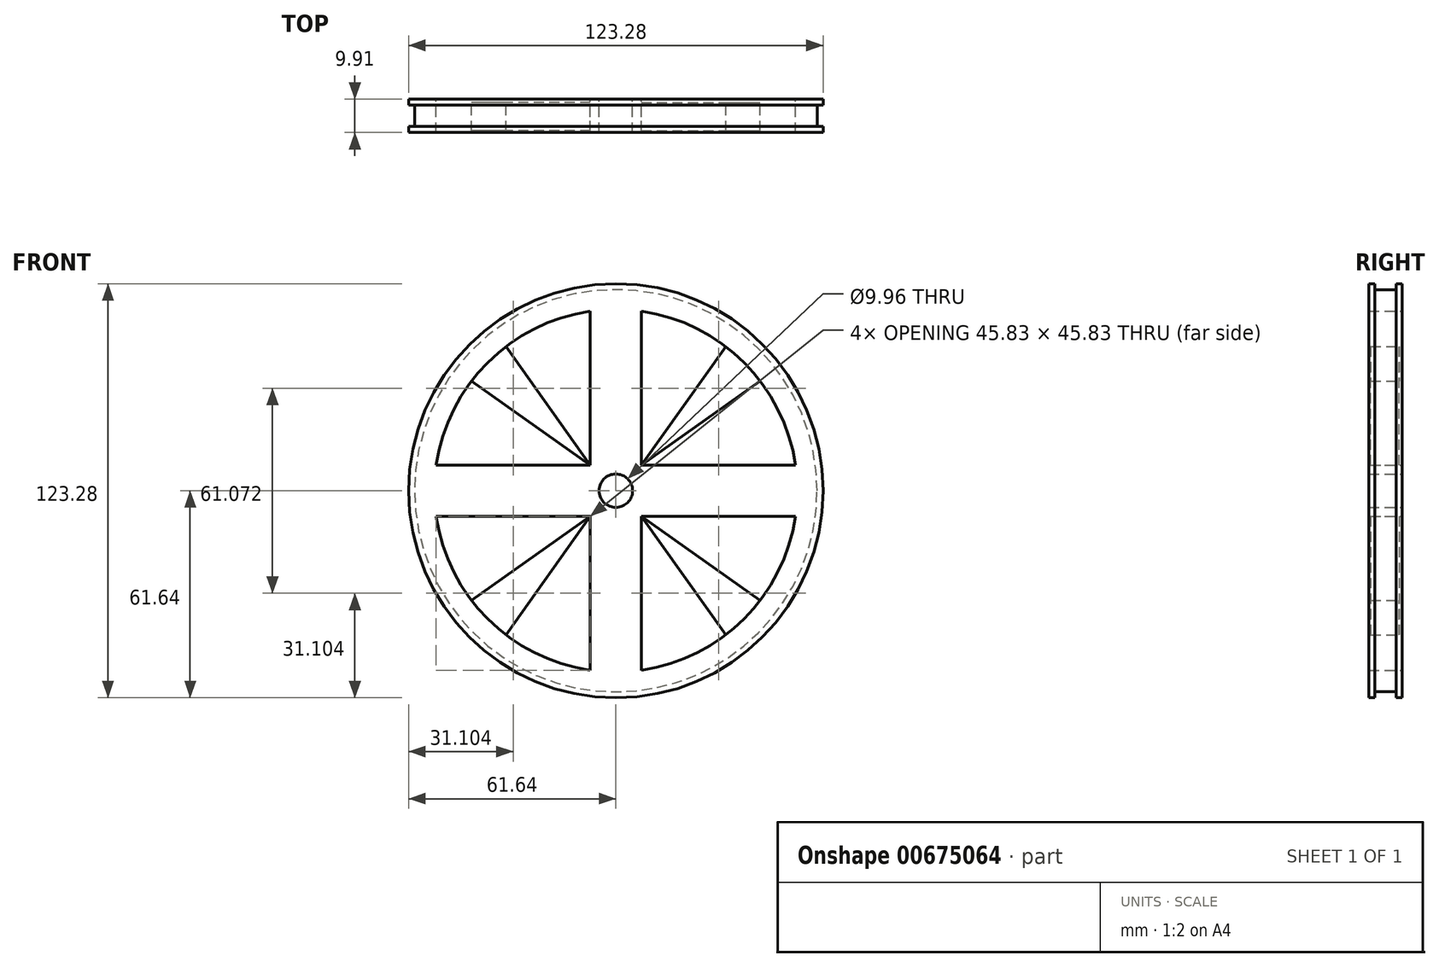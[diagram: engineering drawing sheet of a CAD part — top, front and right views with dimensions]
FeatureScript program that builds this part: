
annotation { "Feature Type Name" : "Feature", "Feature Type Description" : "" }
export const myFeature = defineFeature(function(context is Context, id is Id, definition is map)
    precondition{}
    {
        {
            var Q0;
            Q0=qCreatedBy(makeId("Front.planeOp"),FACE);
            var sketch = newSketch(context, id + "F0", { "sketchPlane" : qUnion([Q0])});
            skCircle(sketch, "E0", {"center": v(0, 0) * mm, "radius": 61.64 * mm});
            skLineSegment(sketch, "E1", {"start": v(-61.64, 0) * mm, "end": v(0, 0) * mm});
            skLineSegment(sketch, "E2", {"start": v(0, 0) * mm, "end": v(0, 61.64) * mm});
            skPoint(sketch, "E3", {"position": v(-61.64, 0) * mm});
            skPoint(sketch, "E4", {"position": v(0, 61.64) * mm});
            skArc(sketch, "E5", {"start": v(0, 61.64) * mm, "mid": v(-43.52, 43.52) * mm, "end": v(-61.64, 0) * mm});
            skArc(sketch, "E6.0", {"start": v(-7.62, 53.45) * mm, "mid": v(-38.14, 38.14) * mm, "end": v(-53.45, 7.62) * mm});
            skLineSegment(sketch, "E6.1", {"start": v(-7.62, 7.62) * mm, "end": v(-7.62, 53.45) * mm});
            skLineSegment(sketch, "E6.2", {"start": v(-53.45, 7.62) * mm, "end": v(-7.62, 7.62) * mm});
            skArc(sketch, "E7.1.0", {"start": v(-53.45, -7.62) * mm, "mid": v(-38.14, -38.14) * mm, "end": v(-7.62, -53.45) * mm});
            skLineSegment(sketch, "E7.1.1", {"start": v(-7.62, -7.62) * mm, "end": v(-53.45, -7.62) * mm});
            skLineSegment(sketch, "E7.1.2", {"start": v(-7.62, -53.45) * mm, "end": v(-7.62, -7.62) * mm});
            skArc(sketch, "E7.2.0", {"start": v(7.62, -53.45) * mm, "mid": v(38.14, -38.14) * mm, "end": v(53.45, -7.62) * mm});
            skLineSegment(sketch, "E7.2.1", {"start": v(7.62, -7.62) * mm, "end": v(7.62, -53.45) * mm});
            skLineSegment(sketch, "E7.2.2", {"start": v(53.45, -7.62) * mm, "end": v(7.62, -7.62) * mm});
            skArc(sketch, "E7.3.0", {"start": v(53.45, 7.62) * mm, "mid": v(38.14, 38.14) * mm, "end": v(7.62, 53.45) * mm});
            skLineSegment(sketch, "E7.3.1", {"start": v(7.62, 7.62) * mm, "end": v(53.45, 7.62) * mm});
            skLineSegment(sketch, "E7.3.2", {"start": v(7.62, 53.45) * mm, "end": v(7.62, 7.62) * mm});
            skLineSegment(sketch, "E8", {"start": v(-7.62, 7.62) * mm, "end": v(-32.68, 42.9) * mm});
            skLineSegment(sketch, "E9", {"start": v(-7.62, 7.62) * mm, "end": v(-42.9, 32.68) * mm});
            skLineSegment(sketch, "E10.1.0", {"start": v(-7.62, -7.62) * mm, "end": v(-42.9, -32.68) * mm});
            skLineSegment(sketch, "E10.1.1", {"start": v(-7.62, -7.62) * mm, "end": v(-32.68, -42.9) * mm});
            skLineSegment(sketch, "E10.2.0", {"start": v(7.62, -7.62) * mm, "end": v(32.68, -42.9) * mm});
            skLineSegment(sketch, "E10.2.1", {"start": v(7.62, -7.62) * mm, "end": v(42.9, -32.68) * mm});
            skLineSegment(sketch, "E10.3.0", {"start": v(7.62, 7.62) * mm, "end": v(42.9, 32.68) * mm});
            skLineSegment(sketch, "E10.3.1", {"start": v(7.62, 7.62) * mm, "end": v(32.68, 42.9) * mm});
            skSolve(sketch);
        }
        {
            var Q0;
            Q0=makeQuery(id+"F0.imprint","IMPRINT",FACE,{"disambiguationData":[TD([[makeQuery(id+"F0.imprint","IMPRINT",EDGE,{"derivedFrom":sQuery(id+"F0.wireOp",EDGE,"E1")}),1.0]])]});
            var Q1;
            {var subQ1=sQuery(id+"F0.wireOp",EDGE,"E1");Q1=makeQuery(id+"F0.imprint","IMPRINT",FACE,{"disambiguationData":[TD([[makeQuery(id+"F0.imprint","IMPRINT",EDGE,{"derivedFrom":subQ1}),-1.0]])]});}
            extrude(context, id + "F1", {"entities" : qUnion([Q0, Q1]), "depth" : 9.9 * mm, "offsetDistance" : 25.4 * mm});
        }
        {
            var Q0;
            Q0=makeQuery(id+"F1.opExtrude","CAP_FACE",FACE,{"disambiguationData":[OSD([sQuery(id+"F0.wireOp",EDGE,"E0"),sQuery(id+"F0.wireOp",EDGE,"E5"),sQuery(id+"F0.wireOp",EDGE,"E6.0"),sQuery(id+"F0.wireOp",EDGE,"E6.1"),sQuery(id+"F0.wireOp",EDGE,"E6.2"),sQuery(id+"F0.wireOp",EDGE,"E7.1.0"),sQuery(id+"F0.wireOp",EDGE,"E7.1.1"),sQuery(id+"F0.wireOp",EDGE,"E7.1.2"),sQuery(id+"F0.wireOp",EDGE,"E7.2.0"),sQuery(id+"F0.wireOp",EDGE,"E7.2.1"),sQuery(id+"F0.wireOp",EDGE,"E7.2.2"),sQuery(id+"F0.wireOp",EDGE,"E7.3.0"),sQuery(id+"F0.wireOp",EDGE,"E7.3.1"),sQuery(id+"F0.wireOp",EDGE,"E7.3.2")])],"isStart":true});
            var sketch = newSketch(context, id + "F2", { "sketchPlane" : qUnion([Q0])});
            skCircle(sketch, "E11", {"center": v(0, 0) * mm, "radius": 4.98 * mm});
            skSolve(sketch);
        }
        {
            var Q0;
            Q0=makeQuery(id+"F2.imprint","IMPRINT",FACE,{"disambiguationData":[TD([[makeQuery(id+"F2.imprint","IMPRINT",EDGE,{"derivedFrom":sQuery(id+"F2.wireOp",EDGE,"E11")}),1.0]])]});
            extrude(context, id + "F3", {"entities" : qUnion([Q0]), "operationType" : NewBodyOperationType.REMOVE, "oppositeDirection" : true, "depth" : 25.4 * mm, "offsetDistance" : 25.4 * mm});
        }
        {
            var Q0;
            {var subQ0=sQuery(id+"F0.wireOp",EDGE,"E8");Q0=makeQuery(id+"F0.imprint","IMPRINT",FACE,{"disambiguationData":[TD([[makeQuery(id+"F0.imprint","IMPRINT",EDGE,{"derivedFrom":subQ0}),1.0]])]});}
            var Q1;
            {var subQ0=sQuery(id+"F0.wireOp",EDGE,"E10.1.0");Q1=makeQuery(id+"F0.imprint","IMPRINT",FACE,{"disambiguationData":[TD([[makeQuery(id+"F0.imprint","IMPRINT",EDGE,{"derivedFrom":subQ0}),1.0]])]});}
            var Q2;
            {var subQ0=sQuery(id+"F0.wireOp",EDGE,"E10.2.0");Q2=makeQuery(id+"F0.imprint","IMPRINT",FACE,{"disambiguationData":[TD([[makeQuery(id+"F0.imprint","IMPRINT",EDGE,{"derivedFrom":subQ0}),1.0]])]});}
            var Q3;
            {var subQ0=sQuery(id+"F0.wireOp",EDGE,"E10.3.0");Q3=makeQuery(id+"F0.imprint","IMPRINT",FACE,{"disambiguationData":[TD([[makeQuery(id+"F0.imprint","IMPRINT",EDGE,{"derivedFrom":subQ0}),1.0]])]});}
            extrude(context, id + "F4", {"entities" : qUnion([Q0, Q1, Q2, Q3]), "depth" : 9.4 * mm, "offsetDistance" : 25.4 * mm, "hasSecondDirection" : true, "secondDirectionOppositeDirection" : false, "secondDirectionDepth" : 0.97 * mm});
        }
        {
            var Q0;
            Q0=qCreatedBy(makeId("Right.planeOp"),FACE);
            var sketch = newSketch(context, id + "F5", { "sketchPlane" : qUnion([Q0])});
            skLineSegment(sketch, "E12", {"start": v(36.85, 0) * mm, "end": v(-75.67, 0) * mm});
            skLineSegment(sketch, "E13.bottom", {"start": v(-1.78, 61.64) * mm, "end": v(-8.13, 61.64) * mm});
            skLineSegment(sketch, "E13.top", {"start": v(-1.78, 59.86) * mm, "end": v(-8.13, 59.86) * mm});
            skLineSegment(sketch, "E13.left", {"start": v(-1.78, 61.64) * mm, "end": v(-1.78, 59.86) * mm});
            skLineSegment(sketch, "E13.right", {"start": v(-8.13, 61.64) * mm, "end": v(-8.13, 59.86) * mm});
            skLineSegment(sketch, "E14.MirrorCS", {"start": v(-1.78, -61.64) * mm, "end": v(-8.13, -61.64) * mm});
            skLineSegment(sketch, "E15.MirrorCS", {"start": v(-8.13, -61.64) * mm, "end": v(-8.13, -59.86) * mm});
            skLineSegment(sketch, "E16.MirrorCS", {"start": v(-1.78, -59.86) * mm, "end": v(-8.13, -59.86) * mm});
            skLineSegment(sketch, "E17.MirrorCS", {"start": v(-1.78, -61.64) * mm, "end": v(-1.78, -59.86) * mm});
            skSolve(sketch);
        }
        {
            var Q0;
            Q0=makeQuery(id+"F5.imprint","IMPRINT",FACE,{"disambiguationData":[TD([[makeQuery(id+"F5.imprint","IMPRINT",EDGE,{"derivedFrom":sQuery(id+"F5.wireOp",EDGE,"E13.bottom")}),1.0]])]});
            var Q1;
            Q1=sQuery(id+"F5.wireOp",EDGE,"E12");
            revolve(context, id + "F6", {"operationType" : NewBodyOperationType.REMOVE, "entities" : qUnion([Q0]), "axis" : qUnion([Q1]), "revolveType" : RevolveType.FULL, "oppositeDirection" : true});
        }
    });
